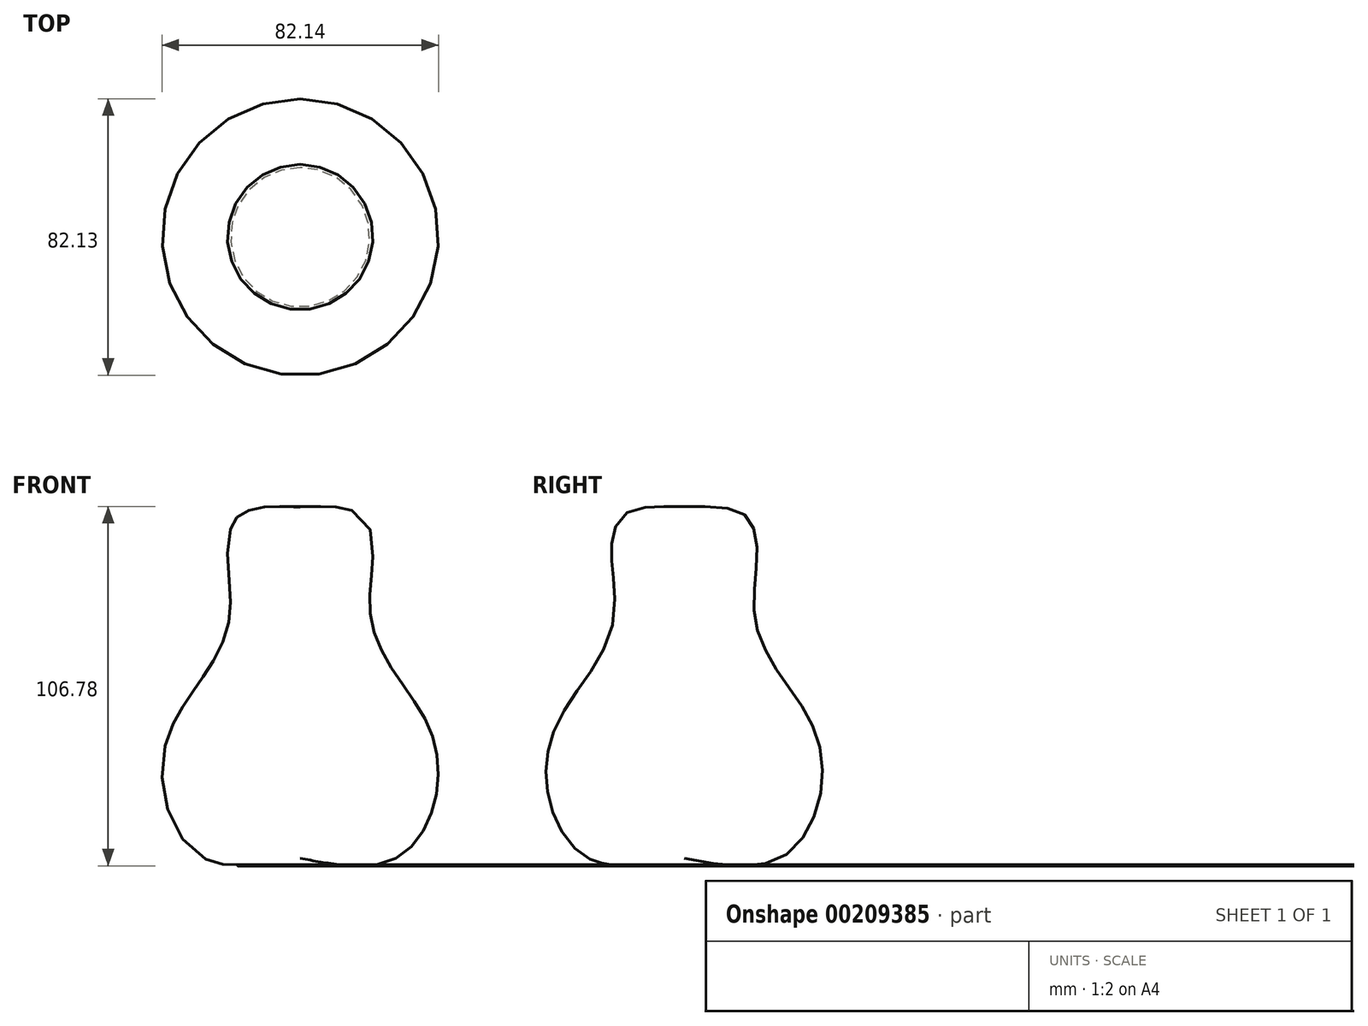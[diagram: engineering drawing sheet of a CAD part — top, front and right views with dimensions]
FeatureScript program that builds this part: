
annotation { "Feature Type Name" : "Feature", "Feature Type Description" : "" }
export const myFeature = defineFeature(function(context is Context, id is Id, definition is map)
    precondition{}
    {
        {
            var Q0;
            Q0=qCreatedBy(makeId("Right.planeOp"),FACE);
            var sketch = newSketch(context, id + "F0", { "sketchPlane" : qUnion([Q0])});
            skFitSpline(sketch, "E0", {"points": [v(0, -65.8) * mm, v(27.82, -66.11) * mm, v(40.01, -48.92) * mm, v(38.76, -27.98) * mm, v(28.13, -10.78) * mm, v(20.94, 5.78) * mm, v(21.57, 23.6) * mm, v(18.13, 36.1) * mm, v(0, 38.6) * mm], "startDerivative": vector(206.15, -37.6) * mm, "endDerivative": vector(-179.08, -6.65) * mm});
            skLineSegment(sketch, "E1", {"start": v(0, -62.53) * mm, "end": v(0, -74.33) * mm});
            skSolve(sketch);
        }
        {
            var Q0;
            Q0=sQuery(id+"F0.wireOp",EDGE,"E0");
            var Q1;
            Q1=sQuery(id+"F0.wireOp",EDGE,"E1");
            revolve(context, id + "F1", {"bodyType" : ToolBodyType.SURFACE, "surfaceEntities" : qUnion([Q0]), "axis" : qUnion([Q1]), "revolveType" : RevolveType.FULL});
        }
    });
